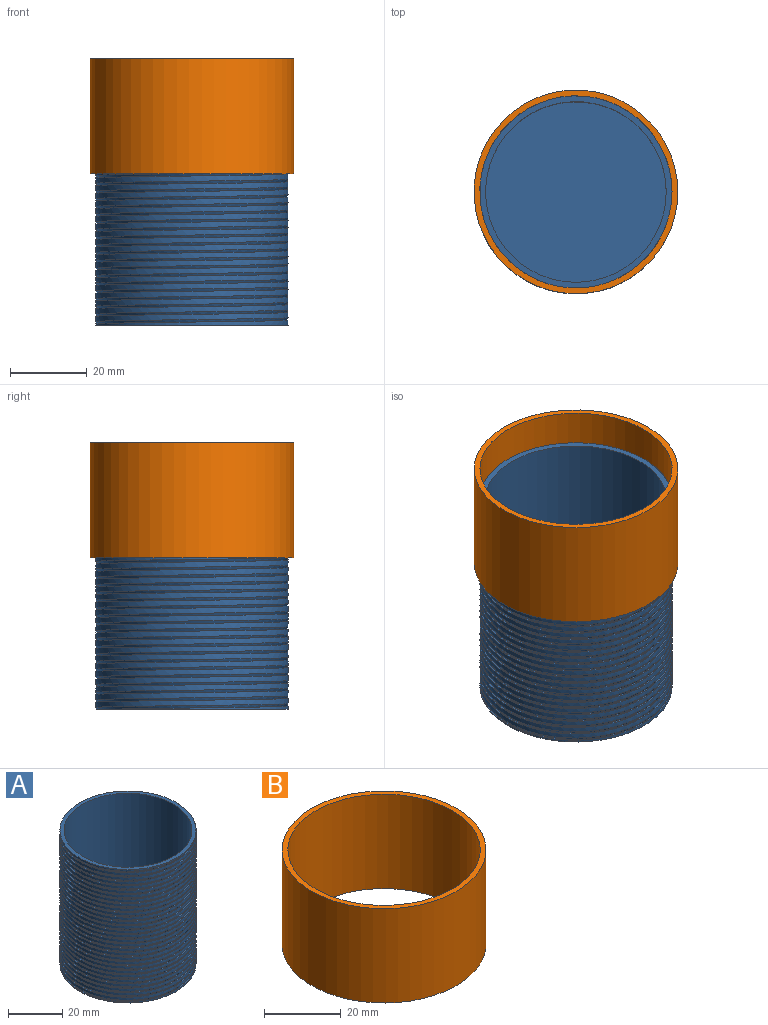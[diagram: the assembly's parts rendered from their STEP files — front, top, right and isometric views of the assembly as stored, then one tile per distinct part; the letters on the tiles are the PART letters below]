
ASSEMBLY  parts=2 mates=1
PART A: 8 faces, bbox 51.4x59.3x61 mm
  f0: cylinder r=25mm len=60mm, axis (0,0,-1), area 8603.9mm2, adj f1,f2,f5,f6,f7
  f1: plane 50x50mm, normal (0,0,1), area 228.6mm2, adj f0,f3
  f2: plane 50.35x50.08mm, normal (0,0,-1), area 1954.8mm2, adj f0,f6,f7
  f3: cylinder r=23.5mm len=47mm, axis (0,0,1), area 6939.8mm2, adj f1,f4
  f4: plane 47x47mm, normal (0,0,1), area 1734.9mm2, adj f3
  f5: plane 0.64x0.35mm, normal (0,-1,0), area 0.1mm2, adj f0,f6,f7
  f6: bspline ~60.64x57.74mm, area 3380mm2, adj f0,f2,f5,f7
  f7: bspline ~59.67x58.91mm, area 1625.2mm2, adj f0,f2,f5,f6
PART B: 4 faces, bbox 53x53x30 mm
  f0: cylinder r=26.5mm len=53mm, axis (0,0,-1), area 4995.1mm2, adj f1,f2
  f1: plane 53x53mm, normal (0,0,1), area 242.7mm2, adj f0,f3
  f2: plane 53x53mm, normal (0,0,-1), area 242.7mm2, adj f0,f3
  f3: cylinder r=25mm len=50mm, axis (0,0,1), area 4712.4mm2, adj f1,f2
PLACE A t=(-0.04,0,-25.18)mm fixed
PLACE B rot(axis=(0,0,-1),63.3deg) t=(-0.04,0,14.22)mm
MATE cylindrical A.f3 <-> B.f0  axis (0,0,1) through (-0.04,0,34.82)mm
